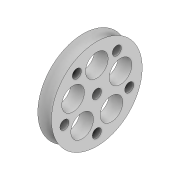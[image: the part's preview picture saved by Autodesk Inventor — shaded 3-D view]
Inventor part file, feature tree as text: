
AUTODESK INVENTOR PART (.ipt)
format: ipt  version: 2022 (Build 260153000, 153)  size: 155,648 bytes
history: native  units: mm
features: sketch x3, extrude x2, revolve x1, pattern_circular x1
ambient origin geometry x8: Origin, YZ Plane, XZ Plane, XY Plane, X Axis, Y Axis, Z Axis, Center Point
bodies: Solid1 (feature_tree)
feature tree (7):
  revolve  "Revolution1"  [1 undecoded]
  extrude  "Extrusion1"  TaperAngle=360.0deg  [1 undecoded]
  extrude  "Extrusion2"  Depth=10.0mm TaperAngle=0.0deg
  pattern_circular  "Circular Pattern1"  [2 undecoded]
  sketch  "Sketch1"  dims[d0=6.0mm d1=3.0mm]
  sketch  "Sketch2"  dims[d2=20.0mm d4=360.0deg]
  sketch  "Sketch3"  dims[d5=4.1mm d6=10.0mm d7=0.0mm d8=10.0mm d9=11.0mm d10=100.0mm d11=0.0mm d12=50.0mm d13=360.0deg d16=3.3mm d17=4.0mm d18=15.0mm d19=6.283185mm]
note: 4 required parameter values undecoded (feature->parameter linkage not recoverable at this tier; creation-order binding heuristic only, values carry confidence <= 0.55)